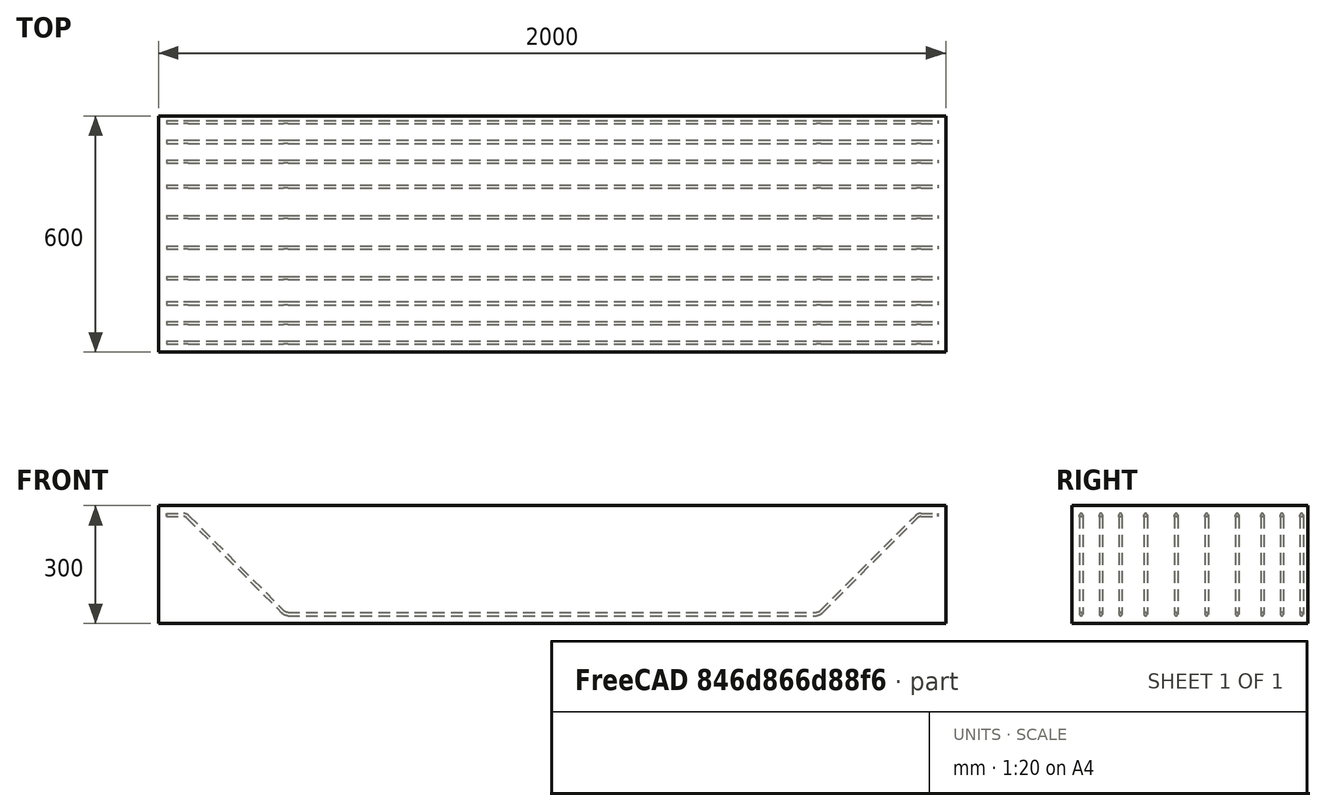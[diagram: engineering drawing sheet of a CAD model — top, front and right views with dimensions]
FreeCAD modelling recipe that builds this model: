
FCSTD DOCUMENT  (FreeCAD 0.19R20802 (Git))
Label: bent_rebar_drawing_dimension
License: All rights reserved
LicenseURL: http://en.wikipedia.org/wiki/All_rights_reserved
objects: TechDraw::DrawViewSymbolPython×12, TechDraw::DrawSVGTemplate×6, TechDraw::DrawPage×6, Part::FeaturePython×2, Sketcher::SketchObject×1
note: 3 computed .brp shape members not serialized (recipe doc carries the construction recipe); baked Part::Feature solids carry a one-line shape summary decoded from their .brp

FEATURE [Part::FeaturePython] Structure  label="Beam"  # Arch/BIM 7 (typed FeaturePython)
  FaceMaker = 0
  Height = 300
  HorizontalArea = 1200000
  IfcData = attributes={"GlobalId": {"name": "GlobalId", "type": "IfcGloballyUniqueId", "is_enum": false, "enum_values": []}, "Description": {"... (+475 chars omitted),+1 more (map truncated)
  IfcType = 7
  Length = 2000
  MoveBase = false
  MoveWithHost = false
  Nodes = (2) [(0,-3.03165e-15,5.55112e-16),(0,-3.03165e-15,2000)]
  NodesOffset = 0
  Normal = (0,0,0)
  PerimeterLength = 5200
  Placement = pos=(-2.63138,-0.01932,0) rot=(0,0,1;0rad)
  PredefinedType = 0
  VerticalArea = 1560000
  Width = 600
FEATURE [Sketcher::SketchObject] Sketch
  MapMode = 5
  Placement = pos=(-2.63138,-300.019,0) rot=(1,0,0;1.5708rad)
  Support = -> [Structure]
  sketch-geometry (5):
    g0: LineSegment StartX=20 StartY=126 StartZ=0 EndX=70 EndY=126 EndZ=0
    g1: LineSegment StartX=70 StartY=126 StartZ=0 EndX=322 EndY=-126 EndZ=0
    g2: LineSegment StartX=322 StartY=-126 StartZ=0 EndX=1678 EndY=-126 EndZ=0
    g3: LineSegment StartX=1678 StartY=-126 StartZ=0 EndX=1930 EndY=126 EndZ=0
    g4: LineSegment StartX=1930 StartY=126 StartZ=0 EndX=1980 EndY=126 EndZ=0
FEATURE [Part::FeaturePython] Rebar  label="BentShapeRebar"  # Arch/BIM 110 (typed FeaturePython)
  Amount = 10
  AmountCheck = false
  Base = -> Sketch
  BentAngle = 135
  BentLength = 50
  BottomCover = 20
  CustomSpacing = 3@50.0+4@77.5+3@50.0
  Diameter = 8
  Direction = (0,0,0)
  Distance = 0
  FrontCover = 20
  HorizontalArea = 0
  Host = -> Structure
  IfcType = 110
  LeftCover = 20
  Length = 2168.76
  Mark = BR
  MoveBase = false
  MoveWithHost = false
  OffsetEnd = 24
  OffsetStart = 24
  Orientation = Bottom
  PerimeterLength = 0
  PlacementList = 10 placements: [(0,24,-5.32907e-15),(0,74,-1.64313e-14),(0,124,-2.75335e-14),(0,187.75,-4.16889e-14),(0,265.25,-5.88973e-14),(0,342.75,-7.61058e-14),(0,420.25,-9.33142e-14),(0,484,-1.0747e-13),(0,534,-1.18572e-13),(0,584,-1.29674e-13)]
  RebarShape = 4
  RightCover = 20
  Rounding = 2
  Spacing = 0
  TopCover = 20
  TotalLength = 21687.6
  TrueSpacing = 50
  VerticalArea = 0
FEATURE [TechDraw::DrawSVGTemplate] Template
  Height = 210
  Orientation = 1
  Width = 297
FEATURE [TechDraw::DrawViewSymbolPython] ReinforcementDrawingView  label="Front View"  # drawing view (typed FeaturePython)
  DimensionBottomOffset = 16
  DimensionLeftOffset = 10
  DimensionRightOffset = 10
  DimensionTopOffset = 10
  Height = 300
  LeftOffset = 20
  LockPosition = false
  MaxHeight = 210
  MaxWidth = 297
  MinBottomOffset = 20
  MinRightOffset = 20
  PositionType = 0
  Rebars = -> [Rebar]
  RebarsColorStyle = 0
  RebarsStrokeWidth = 0.35
  Rotation = 0
  Scale = 0.1285
  ScaleType = 1
  Structure = -> Structure
  StructureColorStyle = 0
  StructureStrokeWidth = 0.5
  Symbol = <blob: 3950 chars omitted>
  Template = -> Template
  TopOffset = 85.725
  View = 0
  VisibleRebars = -> [Rebar]
  Width = 2000
  X = 148.5
  Y = 105
  expr: TopOffset = .Template.Height.Value / 2 - .Height.Value * .Scale / 2
  expr: LeftOffset = .Template.Width.Value / 2 - .Width.Value * .Scale / 2
FEATURE [TechDraw::DrawViewSymbolPython] ReinforcementDimensioning  # drawing view (typed FeaturePython)
  DimensionBottomOffset = 10
  DimensionFormat = %M %C⌀%D,span=%S
  DimensionLeftOffset = 10
  DimensionRightOffset = 10
  DimensionTopOffset = 10
  Font = DejaVu Sans
  FontSize = 3
  LineEndSymbol = 0
  LineMidPointSymbol = 1
  LineStartSymbol = 3
  LineStyle = 0
  LockPosition = false
  MultiRebar_LineEndSymbol = 0
  MultiRebar_LineStartSymbol = 0
  MultiRebar_OuterDimension = true
  MultiRebar_TextPositionType = 0
  ParentDrawingView = -> ReinforcementDrawingView
  Rebar = -> Rebar
  Rotation = 0
  Scale = 0.1285
  ScaleType = 2
  SingleRebar_LineEndSymbol = 0
  SingleRebar_LineStartSymbol = 3
  SingleRebar_OuterDimension = false
  SingleRebar_TextPositionType = 1
  StrokeWidth = 0.25
  Symbol = <svg version="1.1" xmlns="http://www.w3.org/2000/svg" xmlns:xlink="http://www.w3.org/1999/xlink" xmlns:freecad="http://www.freecadweb.org/wiki/index.php?title=Svg_Namespace" width="2000.0mm" height="300.0mm" viewBox="0 0 2000.0 300.0"><g transform="translate(2.631375789642334, 150.00000000000045)"><g><path d="M1064.0 227.82101167315176 L1064.0 125.99999999999977" style="stroke:#00007f;stroke-width:1.9455252918287937;stroke-linecap:round;fill:none;" stroke-dasharray="" /><g id="line_mid_points" /><path d="M0,0 -8,-1.5 V1.5 L0,0" style="stroke:#00007f;fill:#00007f;stroke-width:1.9455252918287937;stroke-linecap:round;stroke-linejoin:bevel;" transform="translate(1064.0 125.99999999999977) rotate(-90.0 0 0)" /></g><text x="1064.0" y="239.4941634241245" style="white-space:pre;" fill="#005400" font-family="DejaVu Sans" font-size="23.346303501945524" text-anchor="middle" dominant-baseline="baseline" xml:space="preserve">BR 10⌀8,span=560</text></g></svg>
  TextPositionType = 0
  WayPoints = (2) [(0,0,0),(50,0,0)]
  WayPointsType = 0
  X = 148.5
  Y = 105
FEATURE [TechDraw::DrawPage] TechDraw__DrawPage  label="Beam Drawing"
  KeepUpdated = true
  NextBalloonIndex = 1
  ProjectionType = 0
  Template = -> Template
  Views = -> [ReinforcementDrawingView,ReinforcementDimensioning]
FEATURE [TechDraw::DrawSVGTemplate] Template001
  Height = 210
  Orientation = 1
  Width = 297
FEATURE [TechDraw::DrawViewSymbolPython] ReinforcementDrawingView001  label="Rear View"  # drawing view (typed FeaturePython)
  DimensionBottomOffset = 16
  DimensionLeftOffset = 10
  DimensionRightOffset = 10
  DimensionTopOffset = 10
  Height = 300
  LeftOffset = 20
  LockPosition = false
  MaxHeight = 210
  MaxWidth = 297
  MinBottomOffset = 20
  MinRightOffset = 20
  PositionType = 0
  Rebars = -> [Rebar]
  RebarsColorStyle = 0
  RebarsStrokeWidth = 0.35
  Rotation = 0
  Scale = 0.1285
  ScaleType = 1
  Structure = -> Structure
  StructureColorStyle = 0
  StructureStrokeWidth = 0.5
  Symbol = <blob: 3967 chars omitted>
  Template = -> Template001
  TopOffset = 85.725
  View = 1
  VisibleRebars = -> [Rebar]
  Width = 2000
  X = 148.5
  Y = 105
  expr: TopOffset = .Template.Height.Value / 2 - .Height.Value * .Scale / 2
  expr: LeftOffset = .Template.Width.Value / 2 - .Width.Value * .Scale / 2
FEATURE [TechDraw::DrawViewSymbolPython] ReinforcementDimensioning001  # drawing view (typed FeaturePython)
  DimensionBottomOffset = 10
  DimensionFormat = %M %C⌀%D,span=%S
  DimensionLeftOffset = 10
  DimensionRightOffset = 10
  DimensionTopOffset = 10
  Font = DejaVu Sans
  FontSize = 3
  LineEndSymbol = 0
  LineMidPointSymbol = 1
  LineStartSymbol = 3
  LineStyle = 0
  LockPosition = false
  MultiRebar_LineEndSymbol = 0
  MultiRebar_LineStartSymbol = 0
  MultiRebar_OuterDimension = true
  MultiRebar_TextPositionType = 0
  ParentDrawingView = -> ReinforcementDrawingView001
  Rebar = -> Rebar
  Rotation = 0
  Scale = 0.1285
  ScaleType = 2
  SingleRebar_LineEndSymbol = 0
  SingleRebar_LineStartSymbol = 3
  SingleRebar_OuterDimension = false
  SingleRebar_TextPositionType = 1
  StrokeWidth = 0.25
  Symbol = <svg version="1.1" xmlns="http://www.w3.org/2000/svg" xmlns:xlink="http://www.w3.org/1999/xlink" xmlns:freecad="http://www.freecadweb.org/wiki/index.php?title=Svg_Namespace" width="2000.0mm" height="300.0mm" viewBox="0 0 2000.0 300.0"><g transform="translate(1997.3686242103577, 150.00000000000045)"><g><path d="M-1622.0 227.82101167315176 L-1622.0 125.99999999999977" style="stroke:#00007f;stroke-width:1.9455252918287937;stroke-linecap:round;fill:none;" stroke-dasharray="" /><g id="line_mid_points" /><path d="M0,0 -8,-1.5 V1.5 L0,0" style="stroke:#00007f;fill:#00007f;stroke-width:1.9455252918287937;stroke-linecap:round;stroke-linejoin:bevel;" transform="translate(-1622.0 125.99999999999977) rotate(-90.0 0 0)" /></g><text x="-1622.0" y="239.4941634241245" style="white-space:pre;" fill="#005400" font-family="DejaVu Sans" font-size="23.346303501945524" text-anchor="middle" dominant-baseline="baseline" xml:space="preserve">BR 10⌀8,span=560</text></g></svg>
  TextPositionType = 0
  WayPoints = (2) [(0,0,0),(50,0,0)]
  WayPointsType = 0
  X = 148.5
  Y = 105
FEATURE [TechDraw::DrawPage] TechDraw__DrawPage001  label="Beam Drawing001"
  KeepUpdated = true
  NextBalloonIndex = 1
  ProjectionType = 0
  Template = -> Template001
  Views = -> [ReinforcementDrawingView001,ReinforcementDimensioning001]
FEATURE [TechDraw::DrawSVGTemplate] Template002
  Height = 210
  Orientation = 1
  Width = 297
FEATURE [TechDraw::DrawViewSymbolPython] ReinforcementDrawingView002  label="Left View"  # drawing view (typed FeaturePython)
  DimensionBottomOffset = 16
  DimensionLeftOffset = 10
  DimensionRightOffset = 10
  DimensionTopOffset = 10
  Height = 300
  LeftOffset = 20
  LockPosition = false
  MaxHeight = 210
  MaxWidth = 297
  MinBottomOffset = 20
  MinRightOffset = 20
  PositionType = 0
  Rebars = -> [Rebar]
  RebarsColorStyle = 0
  RebarsStrokeWidth = 0.35
  Rotation = 0
  Scale = 0.428333
  ScaleType = 1
  Structure = -> Structure
  StructureColorStyle = 0
  StructureStrokeWidth = 0.5
  Symbol = <blob: 12051 chars omitted>
  Template = -> Template002
  TopOffset = 40.75
  View = 2
  VisibleRebars = -> [Rebar]
  Width = 600
  X = 148.5
  Y = 105
  expr: TopOffset = .Template.Height.Value / 2 - .Height.Value * .Scale / 2
  expr: LeftOffset = .Template.Width.Value / 2 - .Width.Value * .Scale / 2
FEATURE [TechDraw::DrawViewSymbolPython] ReinforcementDimensioning002  # drawing view (typed FeaturePython)
  DimensionBottomOffset = 10
  DimensionFormat = %M %C⌀%D,span=%S
  DimensionLeftOffset = 10
  DimensionRightOffset = 10
  DimensionTopOffset = 10
  Font = DejaVu Sans
  FontSize = 3
  LineEndSymbol = 0
  LineMidPointSymbol = 1
  LineStartSymbol = 3
  LineStyle = 0
  LockPosition = false
  MultiRebar_LineEndSymbol = 0
  MultiRebar_LineStartSymbol = 0
  MultiRebar_OuterDimension = true
  MultiRebar_TextPositionType = 0
  ParentDrawingView = -> ReinforcementDrawingView002
  Rebar = -> Rebar
  Rotation = 0
  Scale = 0.428333
  ScaleType = 2
  SingleRebar_LineEndSymbol = 0
  SingleRebar_LineStartSymbol = 3
  SingleRebar_OuterDimension = false
  SingleRebar_TextPositionType = 1
  StrokeWidth = 0.25
  Symbol = <blob: 5223 chars omitted>
  TextPositionType = 0
  WayPoints = (2) [(0,0,0),(50,0,0)]
  WayPointsType = 0
  X = 148.5
  Y = 105
FEATURE [TechDraw::DrawPage] TechDraw__DrawPage002  label="Beam Drawing002"
  KeepUpdated = true
  NextBalloonIndex = 1
  ProjectionType = 0
  Template = -> Template002
  Views = -> [ReinforcementDrawingView002,ReinforcementDimensioning002]
FEATURE [TechDraw::DrawSVGTemplate] Template003
  Height = 210
  Orientation = 1
  Width = 297
FEATURE [TechDraw::DrawViewSymbolPython] ReinforcementDrawingView003  label="Right View"  # drawing view (typed FeaturePython)
  DimensionBottomOffset = 16
  DimensionLeftOffset = 10
  DimensionRightOffset = 10
  DimensionTopOffset = 10
  Height = 300
  LeftOffset = 20
  LockPosition = false
  MaxHeight = 210
  MaxWidth = 297
  MinBottomOffset = 20
  MinRightOffset = 20
  PositionType = 0
  Rebars = -> [Rebar]
  RebarsColorStyle = 0
  RebarsStrokeWidth = 0.35
  Rotation = 0
  Scale = 0.428333
  ScaleType = 1
  Structure = -> Structure
  StructureColorStyle = 0
  StructureStrokeWidth = 0.5
  Symbol = <blob: 12051 chars omitted>
  Template = -> Template003
  TopOffset = 40.75
  View = 3
  VisibleRebars = -> [Rebar]
  Width = 600
  X = 148.5
  Y = 105
  expr: TopOffset = .Template.Height.Value / 2 - .Height.Value * .Scale / 2
  expr: LeftOffset = .Template.Width.Value / 2 - .Width.Value * .Scale / 2
FEATURE [TechDraw::DrawViewSymbolPython] ReinforcementDimensioning003  # drawing view (typed FeaturePython)
  DimensionBottomOffset = 10
  DimensionFormat = %M %C⌀%D,span=%S
  DimensionLeftOffset = 10
  DimensionRightOffset = 10
  DimensionTopOffset = 10
  Font = DejaVu Sans
  FontSize = 3
  LineEndSymbol = 0
  LineMidPointSymbol = 1
  LineStartSymbol = 3
  LineStyle = 0
  LockPosition = false
  MultiRebar_LineEndSymbol = 0
  MultiRebar_LineStartSymbol = 0
  MultiRebar_OuterDimension = true
  MultiRebar_TextPositionType = 0
  ParentDrawingView = -> ReinforcementDrawingView003
  Rebar = -> Rebar
  Rotation = 0
  Scale = 0.428333
  ScaleType = 2
  SingleRebar_LineEndSymbol = 0
  SingleRebar_LineStartSymbol = 3
  SingleRebar_OuterDimension = false
  SingleRebar_TextPositionType = 1
  StrokeWidth = 0.25
  Symbol = <blob: 5204 chars omitted>
  TextPositionType = 0
  WayPoints = (2) [(0,0,0),(50,0,0)]
  WayPointsType = 0
  X = 148.5
  Y = 105
FEATURE [TechDraw::DrawPage] TechDraw__DrawPage003  label="Beam Drawing003"
  KeepUpdated = true
  NextBalloonIndex = 1
  ProjectionType = 0
  Template = -> Template003
  Views = -> [ReinforcementDrawingView003,ReinforcementDimensioning003]
FEATURE [TechDraw::DrawSVGTemplate] Template004
  Height = 210
  Orientation = 1
  Width = 297
FEATURE [TechDraw::DrawViewSymbolPython] ReinforcementDrawingView004  label="Top View"  # drawing view (typed FeaturePython)
  DimensionBottomOffset = 10
  DimensionLeftOffset = 10
  DimensionRightOffset = 16
  DimensionTopOffset = 10
  Height = 600
  LeftOffset = 20
  LockPosition = false
  MaxHeight = 210
  MaxWidth = 297
  MinBottomOffset = 20
  MinRightOffset = 20
  PositionType = 0
  Rebars = -> [Rebar]
  RebarsColorStyle = 0
  RebarsStrokeWidth = 0.35
  Rotation = 0
  Scale = 0.1285
  ScaleType = 1
  Structure = -> Structure
  StructureColorStyle = 0
  StructureStrokeWidth = 0.5
  Symbol = <blob: 13697 chars omitted>
  Template = -> Template004
  TopOffset = 66.45
  View = 4
  VisibleRebars = -> [Rebar]
  Width = 2000
  X = 148.5
  Y = 105
  expr: TopOffset = .Template.Height.Value / 2 - .Height.Value * .Scale / 2
  expr: LeftOffset = .Template.Width.Value / 2 - .Width.Value * .Scale / 2
FEATURE [TechDraw::DrawViewSymbolPython] ReinforcementDimensioning004  # drawing view (typed FeaturePython)
  DimensionBottomOffset = 10
  DimensionFormat = %M %C⌀%D,span=%S
  DimensionLeftOffset = 10
  DimensionRightOffset = 10
  DimensionTopOffset = 10
  Font = DejaVu Sans
  FontSize = 3
  LineEndSymbol = 0
  LineMidPointSymbol = 1
  LineStartSymbol = 3
  LineStyle = 0
  LockPosition = false
  MultiRebar_LineEndSymbol = 0
  MultiRebar_LineStartSymbol = 0
  MultiRebar_OuterDimension = true
  MultiRebar_TextPositionType = 0
  ParentDrawingView = -> ReinforcementDrawingView004
  Rebar = -> Rebar
  Rotation = 0
  Scale = 0.1285
  ScaleType = 2
  SingleRebar_LineEndSymbol = 0
  SingleRebar_LineStartSymbol = 3
  SingleRebar_OuterDimension = false
  SingleRebar_TextPositionType = 1
  StrokeWidth = 0.25
  Symbol = <blob: 5216 chars omitted>
  TextPositionType = 0
  WayPoints = (2) [(0,0,0),(50,0,0)]
  WayPointsType = 0
  X = 148.5
  Y = 105
FEATURE [TechDraw::DrawPage] TechDraw__DrawPage004  label="Beam Drawing004"
  KeepUpdated = true
  NextBalloonIndex = 1
  ProjectionType = 0
  Template = -> Template004
  Views = -> [ReinforcementDrawingView004,ReinforcementDimensioning004]
FEATURE [TechDraw::DrawSVGTemplate] Template005
  Height = 210
  Orientation = 1
  Width = 297
FEATURE [TechDraw::DrawViewSymbolPython] ReinforcementDrawingView005  label="Bottom View"  # drawing view (typed FeaturePython)
  DimensionBottomOffset = 10
  DimensionLeftOffset = 10
  DimensionRightOffset = 16
  DimensionTopOffset = 10
  Height = 600
  LeftOffset = 20
  LockPosition = false
  MaxHeight = 210
  MaxWidth = 297
  MinBottomOffset = 20
  MinRightOffset = 20
  PositionType = 0
  Rebars = -> [Rebar]
  RebarsColorStyle = 0
  RebarsStrokeWidth = 0.35
  Rotation = 0
  Scale = 0.1285
  ScaleType = 1
  Structure = -> Structure
  StructureColorStyle = 0
  StructureStrokeWidth = 0.5
  Symbol = <blob: 13697 chars omitted>
  Template = -> Template005
  TopOffset = 66.45
  View = 5
  VisibleRebars = -> [Rebar]
  Width = 2000
  X = 148.5
  Y = 105
  expr: TopOffset = .Template.Height.Value / 2 - .Height.Value * .Scale / 2
  expr: LeftOffset = .Template.Width.Value / 2 - .Width.Value * .Scale / 2
FEATURE [TechDraw::DrawViewSymbolPython] ReinforcementDimensioning005  # drawing view (typed FeaturePython)
  DimensionBottomOffset = 10
  DimensionFormat = %M %C⌀%D,span=%S
  DimensionLeftOffset = 10
  DimensionRightOffset = 10
  DimensionTopOffset = 10
  Font = DejaVu Sans
  FontSize = 3
  LineEndSymbol = 0
  LineMidPointSymbol = 1
  LineStartSymbol = 3
  LineStyle = 0
  LockPosition = false
  MultiRebar_LineEndSymbol = 0
  MultiRebar_LineStartSymbol = 0
  MultiRebar_OuterDimension = true
  MultiRebar_TextPositionType = 0
  ParentDrawingView = -> ReinforcementDrawingView005
  Rebar = -> Rebar
  Rotation = 0
  Scale = 0.1285
  ScaleType = 2
  SingleRebar_LineEndSymbol = 0
  SingleRebar_LineStartSymbol = 3
  SingleRebar_OuterDimension = false
  SingleRebar_TextPositionType = 1
  StrokeWidth = 0.25
  Symbol = <blob: 5211 chars omitted>
  TextPositionType = 0
  WayPoints = (2) [(0,0,0),(50,0,0)]
  WayPointsType = 0
  X = 148.5
  Y = 105
FEATURE [TechDraw::DrawPage] TechDraw__DrawPage005  label="Beam Drawing005"
  KeepUpdated = true
  NextBalloonIndex = 1
  ProjectionType = 0
  Template = -> Template005
  Views = -> [ReinforcementDrawingView005,ReinforcementDimensioning005]
